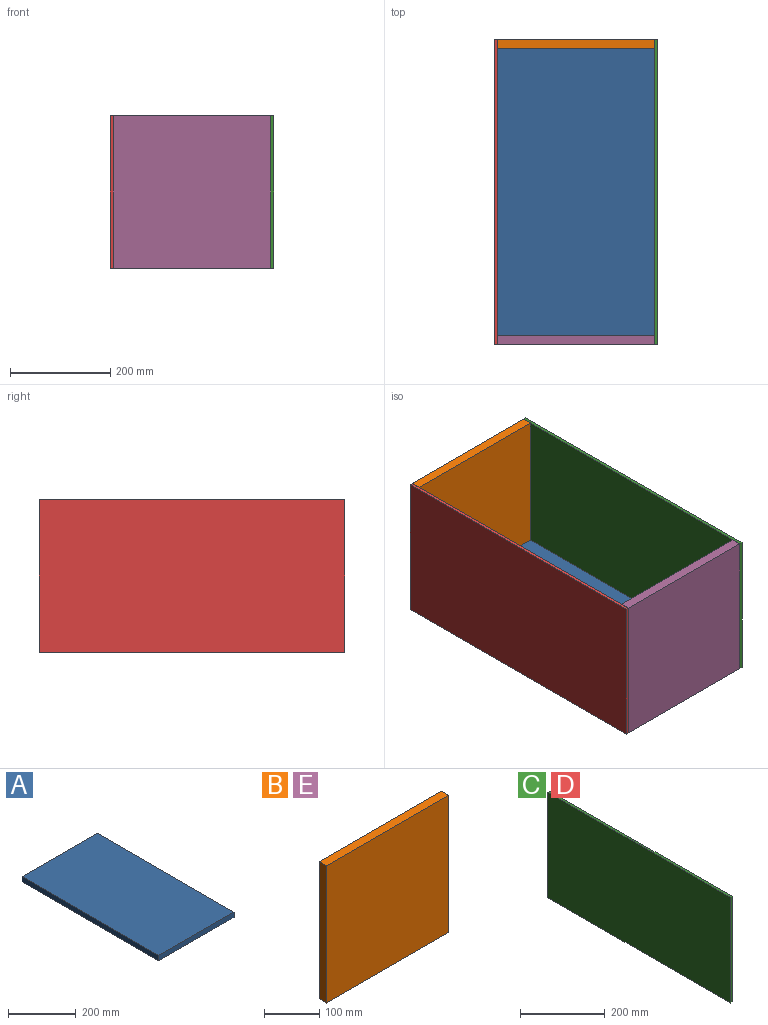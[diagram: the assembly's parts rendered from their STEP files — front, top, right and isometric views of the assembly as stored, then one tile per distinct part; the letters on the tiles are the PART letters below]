
ASSEMBLY  parts=5 mates=6
PART A: 6 faces, bbox 314.3x571.5x19.1 mm
  f0: plane 314.33x19.05mm, normal (0,-1,0), area 5987.9mm2, adj f1,f3,f4,f5
  f1: plane 571.5x19.05mm, normal (1,0,0), area 10887.1mm2, adj f0,f2,f4,f5
  f2: plane 314.33x19.05mm, normal (0,1,0), area 5987.9mm2, adj f1,f3,f4,f5
  f3: plane 571.5x19.05mm, normal (-1,0,0), area 10887.1mm2, adj f0,f2,f4,f5
  f4: plane 571.5x314.33mm, normal (0,0,1), area 179636.7mm2, adj f0,f1,f2,f3
  f5: plane 571.5x314.33mm, normal (0,0,-1), area 179636.7mm2, adj f0,f1,f2,f3
PART B: 6 faces, bbox 314.3x19.1x304.8 mm
  f0: plane 314.33x19.05mm, normal (0,0,-1), area 5987.9mm2, adj f1,f3,f4,f5
  f1: plane 304.8x19.05mm, normal (1,0,0), area 5806.4mm2, adj f0,f2,f4,f5
  f2: plane 314.33x19.05mm, normal (0,0,1), area 5987.9mm2, adj f1,f3,f4,f5
  f3: plane 304.8x19.05mm, normal (-1,0,0), area 5806.4mm2, adj f0,f2,f4,f5
  f4: plane 314.33x304.8mm, normal (0,-1,0), area 95806.3mm2, adj f0,f1,f2,f3
  f5: plane 314.33x304.8mm, normal (0,1,0), area 95806.3mm2, adj f0,f1,f2,f3
PART C: 6 faces, bbox 6.4x609.6x304.8 mm
  f0: plane 304.8x6.35mm, normal (0,-1,0), area 1935.5mm2, adj f1,f3,f4,f5
  f1: plane 609.6x6.35mm, normal (0,0,-1), area 3871mm2, adj f0,f2,f4,f5
  f2: plane 304.8x6.35mm, normal (0,1,0), area 1935.5mm2, adj f1,f3,f4,f5
  f3: plane 609.6x6.35mm, normal (0,0,1), area 3871mm2, adj f0,f2,f4,f5
  f4: plane 609.6x304.8mm, normal (1,0,0), area 185806.1mm2, adj f0,f1,f2,f3
  f5: plane 609.6x304.8mm, normal (-1,0,0), area 185806.1mm2, adj f0,f1,f2,f3
PART D: same geometry as C
PART E: same geometry as B
PLACE A t=(88.06,-269.9,212.96)mm
PLACE B t=(88.06,320.65,212.96)mm
PLACE C t=(88.06,-288.95,212.96)mm
PLACE D t=(-232.61,-288.95,212.96)mm
PLACE E t=(88.06,-269.9,212.96)mm
MATE planar D.f0 <-> E.f4  axis (0,-1,0) through (-229.44,-288.95,365.36)mm
MATE planar D.f1 <-> A.f5  axis (0,0,-1) through (-229.44,15.85,212.96)mm
MATE planar A.f0 <-> E.f5  axis (0,-1,0) through (-69.1,-269.9,222.48)mm
MATE planar A.f3 <-> D.f4  axis (-1,0,0) through (-226.26,15.85,222.48)mm
MATE planar A.f5 <-> E.f0  axis (0,0,-1) through (-69.1,15.85,212.96)mm
MATE planar E.f1 <-> A.f1  axis (1,0,0) through (88.06,-269.9,212.96)mm
